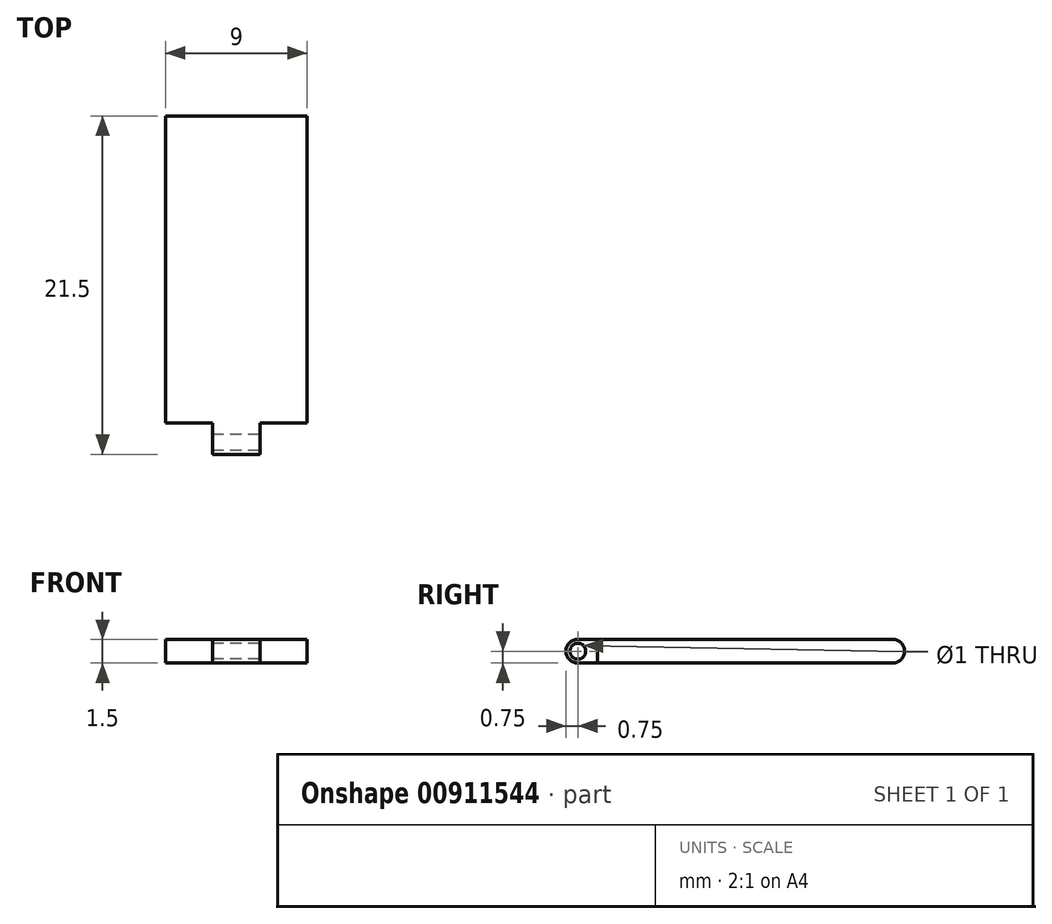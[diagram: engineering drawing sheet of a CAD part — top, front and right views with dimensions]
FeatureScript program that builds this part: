
annotation { "Feature Type Name" : "Feature", "Feature Type Description" : "" }
export const myFeature = defineFeature(function(context is Context, id is Id, definition is map)
    precondition{}
    {
        {
            var Q0;
            Q0=qCreatedBy(makeId("Right.planeOp"),FACE);
            var sketch = newSketch(context, id + "F0", { "sketchPlane" : qUnion([Q0])});
            skLineSegment(sketch, "E0.bottom", {"start": v(0, 0) * mm, "end": v(20, 0) * mm});
            skLineSegment(sketch, "E0.top", {"start": v(0, 1.5) * mm, "end": v(20, 1.5) * mm});
            skLineSegment(sketch, "E0.left", {"start": v(0, 0) * mm, "end": v(0, 1.5) * mm, "construction": true});
            skLineSegment(sketch, "E0.right", {"start": v(20, 0) * mm, "end": v(20, 1.5) * mm, "construction": true});
            skLineSegment(sketch, "E1", {"start": v(0, 0.75) * mm, "end": v(20, 0.75) * mm, "construction": true});
            skArc(sketch, "E2", {"start": v(0, 1.5) * mm, "mid": v(-0.75, 0.75) * mm, "end": v(0, 0) * mm});
            skArc(sketch, "E3", {"start": v(20, 0) * mm, "mid": v(20.75, 0.75) * mm, "end": v(20, 1.5) * mm});
            skCircle(sketch, "E4", {"center": v(0, 0.75) * mm, "radius": 0.5 * mm});
            skSolve(sketch);
        }
        {
            var Q0;
            Q0=qSketchRegion(id+"F0",true);
            extrude(context, id + "F1", {"entities" : qUnion([Q0]), "depth" : 9 * mm, "offsetDistance" : 25 * mm});
        }
        {
            var Q0;
            Q0=qCreatedBy(makeId("Top.planeOp"),FACE);
            var sketch = newSketch(context, id + "F2", { "sketchPlane" : qUnion([Q0])});
            skLineSegment(sketch, "E5.bottom", {"start": v(0, 1.25) * mm, "end": v(3, 1.25) * mm});
            skLineSegment(sketch, "E5.left", {"start": v(0, 1.25) * mm, "end": v(0, -0.75) * mm});
            skLineSegment(sketch, "E5.right", {"start": v(3, 1.25) * mm, "end": v(3, -0.75) * mm});
            skLineSegment(sketch, "E6.bottom", {"start": v(6, 1.25) * mm, "end": v(9, 1.25) * mm});
            skLineSegment(sketch, "E6.left", {"start": v(6, 1.25) * mm, "end": v(6, -0.75) * mm});
            skLineSegment(sketch, "E7.0", {"start": v(9, -0.75) * mm, "end": v(9, 1.25) * mm});
            skLineSegment(sketch, "E8", {"start": v(9, -0.75) * mm, "end": v(6, -0.75) * mm});
            skLineSegment(sketch, "E9.trimOffspring", {"start": v(3, -0.75) * mm, "end": v(0, -0.75) * mm});
            skPoint(sketch, "E10.orphan", {"position": v(9, 0) * mm});
            skPoint(sketch, "E11.orphan", {"position": v(9, 20) * mm});
            skSolve(sketch);
        }
        {
            var Q0;
            Q0 = qSketchRegion(id + "F2", true);
            extrude(context, id + "F3", {"entities" : qUnion([Q0]), "operationType" : NewBodyOperationType.REMOVE, "endBound" : BoundingType.THROUGH_ALL, "depth" : 25 * mm, "offsetDistance" : 25 * mm});
        }
    });
